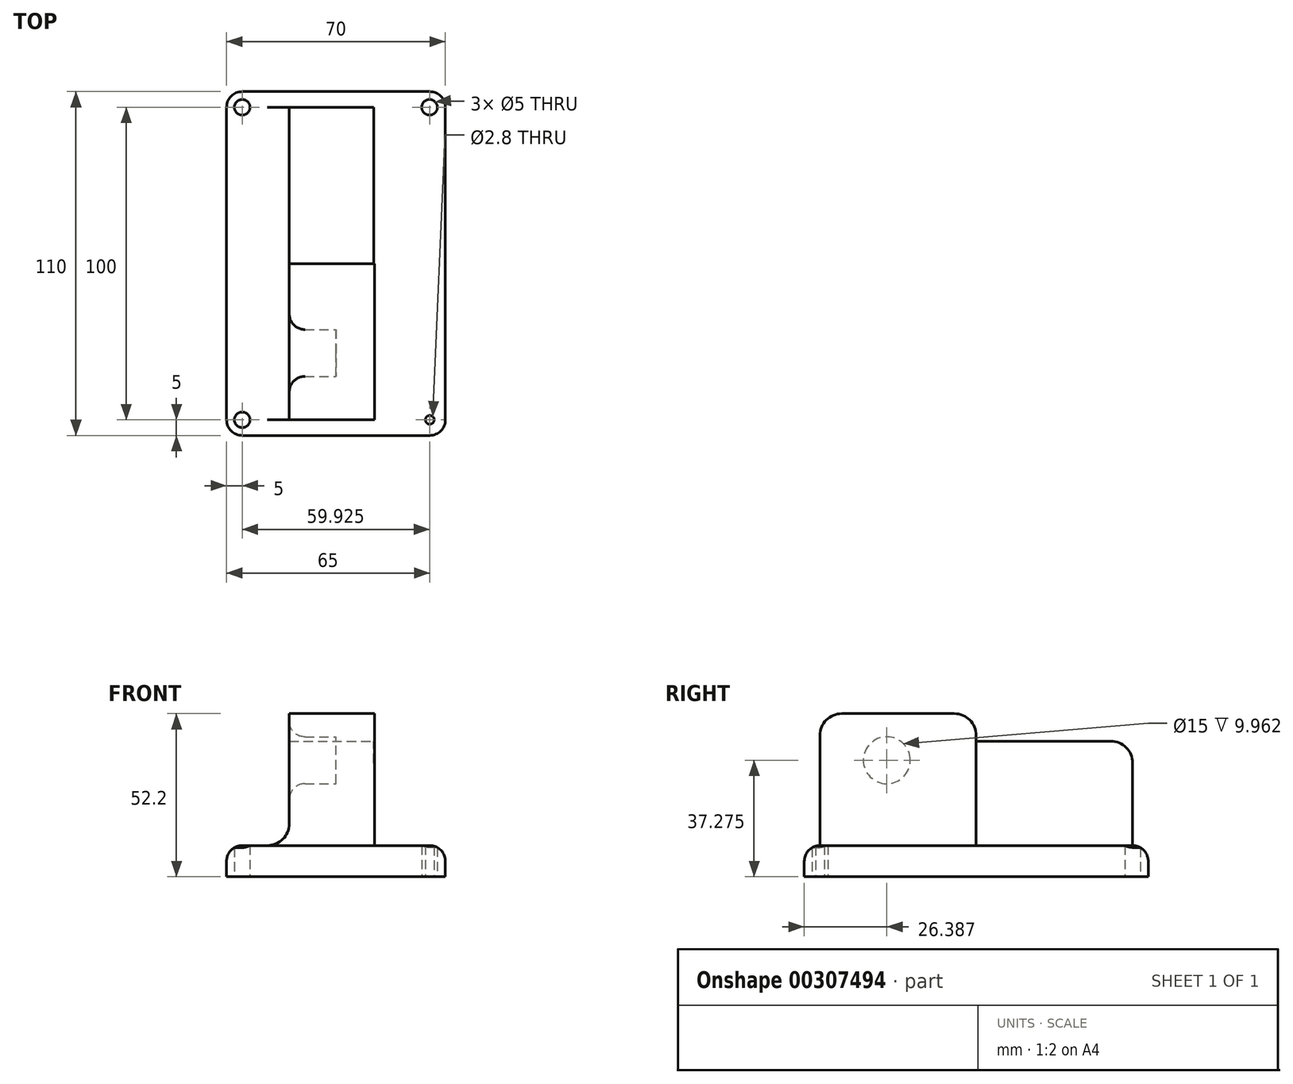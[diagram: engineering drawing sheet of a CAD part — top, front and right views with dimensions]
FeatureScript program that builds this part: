
annotation { "Feature Type Name" : "Feature", "Feature Type Description" : "" }
export const myFeature = defineFeature(function(context is Context, id is Id, definition is map)
    precondition{}
    {
        {
            var Q0;
            Q0=qCreatedBy(makeId("Top.planeOp"),FACE);
            var sketch = newSketch(context, id + "F0", { "sketchPlane" : qUnion([Q0])});
            skLineSegment(sketch, "E0.bottom", {"start": v(30, -55) * mm, "end": v(-30, -55) * mm});
            skLineSegment(sketch, "E0.top", {"start": v(30, 55) * mm, "end": v(-30, 55) * mm});
            skLineSegment(sketch, "E0.left", {"start": v(35, -50) * mm, "end": v(35, 50) * mm});
            skLineSegment(sketch, "E0.right", {"start": v(-35, -50) * mm, "end": v(-35, 50) * mm});
            skPoint(sketch, "E0.middle", {"position": v(0, 0) * mm});
            skPoint(sketch, "E1.visualSharp", {"position": v(-35, 55) * mm});
            skArc(sketch, "E1.filletArc", {"start": v(-30, 55) * mm, "mid": v(-33.54, 53.54) * mm, "end": v(-35, 50) * mm});
            skPoint(sketch, "E2.visualSharp", {"position": v(35, 55) * mm});
            skArc(sketch, "E2.filletArc", {"start": v(35, 50) * mm, "mid": v(33.54, 53.54) * mm, "end": v(30, 55) * mm});
            skPoint(sketch, "E3.visualSharp", {"position": v(35, -55) * mm});
            skArc(sketch, "E3.filletArc", {"start": v(30, -55) * mm, "mid": v(33.54, -53.54) * mm, "end": v(35, -50) * mm});
            skPoint(sketch, "E4.visualSharp", {"position": v(-35, -55) * mm});
            skArc(sketch, "E4.filletArc", {"start": v(-35, -50) * mm, "mid": v(-33.54, -53.54) * mm, "end": v(-30, -55) * mm});
            skLineSegment(sketch, "E5", {"start": v(-35, 50) * mm, "end": v(30, 50) * mm, "construction": true});
            skLineSegment(sketch, "E6", {"start": v(0, 0) * mm, "end": v(0, 50) * mm, "construction": true});
            skLineSegment(sketch, "E7", {"start": v(-30, -50) * mm, "end": v(30, -50) * mm, "construction": true});
            skLineSegment(sketch, "E8.bottom", {"start": v(-14.96, 50) * mm, "end": v(12.07, 50) * mm});
            skLineSegment(sketch, "E8.top", {"start": v(-14.96, 0) * mm, "end": v(12.07, 0) * mm});
            skLineSegment(sketch, "E8.left", {"start": v(-14.96, 50) * mm, "end": v(-14.96, 0) * mm});
            skLineSegment(sketch, "E8.right", {"start": v(12.07, 50) * mm, "end": v(12.07, 0) * mm});
            skLineSegment(sketch, "E9.bottom", {"start": v(-14.96, 0) * mm, "end": v(12.34, 0) * mm});
            skLineSegment(sketch, "E9.top", {"start": v(-14.96, -50) * mm, "end": v(12.34, -50) * mm});
            skLineSegment(sketch, "E9.left", {"start": v(-14.96, 0) * mm, "end": v(-14.96, -50) * mm});
            skLineSegment(sketch, "E9.right", {"start": v(12.34, 0) * mm, "end": v(12.34, -50) * mm});
            skCircle(sketch, "E10", {"center": v(-30, 50) * mm, "radius": 2.5 * mm});
            skCircle(sketch, "E11", {"center": v(29.92, 50) * mm, "radius": 2.5 * mm});
            skCircle(sketch, "E12", {"center": v(-30, -50) * mm, "radius": 2.5 * mm});
            skCircle(sketch, "E13", {"center": v(30, -50) * mm, "radius": 1.4 * mm});
            skSolve(sketch);
        }
        {
            var Q0;
            Q0=makeQuery(id+"F0.imprint","IMPRINT",FACE,{"disambiguationData":[TD([[makeQuery(id+"F0.imprint","IMPRINT",EDGE,{"derivedFrom":sQuery(id+"F0.wireOp",EDGE,"E0.bottom")}),-1.0]])]});
            extrude(context, id + "F1", {"entities" : qUnion([Q0]), "depth" : 10 * mm});
        }
        {
            var Q0;
            Q0=makeQuery(id+"F0.imprint","IMPRINT",FACE,{"disambiguationData":[TD([[makeQuery(id+"F0.imprint","IMPRINT",EDGE,{"derivedFrom":sQuery(id+"F0.wireOp",EDGE,"E8.bottom")}),-1.0]])]});
            extrude(context, id + "F2", {"entities" : qUnion([Q0]), "operationType" : NewBodyOperationType.ADD, "depth" : 43.4 * mm});
        }
        {
            var Q0;
            Q0=makeQuery(id+"F0.imprint","IMPRINT",FACE,{"disambiguationData":[TD([[makeQuery(id+"F0.imprint","IMPRINT",EDGE,{"derivedFrom":sQuery(id+"F0.wireOp",EDGE,"E9.top")}),1.0]])]});
            extrude(context, id + "F3", {"entities" : qUnion([Q0]), "operationType" : NewBodyOperationType.ADD, "depth" : 52.2 * mm});
        }
        {
            var Q0;
            Q0=makeQuery(id+"F3.opExtrude","CAP_EDGE",EDGE,{"disambiguationData":[OSD([sQuery(id+"F0.wireOp",EDGE,"E9.bottom")])],"isStart":false});
            var Q1;
            Q1=makeQuery(id+"F2.opExtrude","CAP_EDGE",EDGE,{"disambiguationData":[OSD([sQuery(id+"F0.wireOp",EDGE,"E8.bottom")])],"isStart":false});
            var Q2;
            Q2=makeQuery(id+"F3.opExtrude","CAP_EDGE",EDGE,{"disambiguationData":[OSD([sQuery(id+"F0.wireOp",EDGE,"E9.top")])],"isStart":false});
            var Q3;
            {var subQ0=sQuery(id+"F0.wireOp",EDGE,"E9.left");var subQ1=sQuery(id+"F0.wireOp",EDGE,"E8.left");var subQ3=makeQuery(id+"F1.opExtrude","CAP_EDGE",EDGE,{"disambiguationData":[OSD([subQ1,subQ0])],"isStart":false});Q3=makeQuery(id+"F3.boolean.opBoolean","MERGE",EDGE,{"derivedFrom":[makeQuery(id+"F2.boolean.opBoolean","SPLIT",EDGE,{"disambiguationData":[topologyDisambiguationEdgeConnected([makeQuery(id+"F1.opExtrude","SWEPT_FACE",FACE,{"disambiguationData":[OSD([subQ1,subQ0])]})])],"derivedFrom":subQ3}),makeQuery(id+"F2.boolean.opBoolean","SPLIT",EDGE,{"disambiguationData":[topologyDisambiguationEdgeConnected([makeQuery(id+"F2.opExtrude","SWEPT_FACE",FACE,{"disambiguationData":[OSD([subQ1])]})])],"derivedFrom":subQ3})]});}
            var Q4;
            Q4=makeQuery(id+"F1.opExtrude","CAP_EDGE",EDGE,{"disambiguationData":[OSD([sQuery(id+"F0.wireOp",EDGE,"E8.bottom")])],"isStart":false});
            fillet(context, id + "F4", {"entities" : qUnion([Q0, Q1, Q2, Q3, Q4]), "radius" : 7 * mm, "tangentPropagation" : true, "allowEdgeOverflow" : false});
        }
        {
            var Q0;
            Q0=qCreatedBy(makeId("Right.planeOp"),FACE);
            var sketch = newSketch(context, id + "F5", { "sketchPlane" : qUnion([Q0])});
            skCircle(sketch, "E14", {"center": v(-28.61, 37.28) * mm, "radius": 7.5 * mm});
            skSolve(sketch);
        }
        {
            var Q0;
            Q0 = qSketchRegion(id + "F5", true);
            extrude(context, id + "F6", {"entities" : qUnion([Q0]), "operationType" : NewBodyOperationType.REMOVE, "oppositeDirection" : true, "depth" : 40 * mm});
        }
        {
            var Q0;
            Q0=makeQuery(id+"F2.opExtrude","CAP_EDGE",EDGE,{"disambiguationData":[OSD([sQuery(id+"F0.wireOp",EDGE,"E8.bottom")])],"isStart":false});
            var Q1;
            Q1=makeQuery(id+"F1.opExtrude","CAP_EDGE",EDGE,{"disambiguationData":[OSD([sQuery(id+"F0.wireOp",EDGE,"E0.right")])],"isStart":false});
            var Q2;
            Q2=makeQuery(id+"F1.opExtrude","CAP_EDGE",EDGE,{"disambiguationData":[OSD([sQuery(id+"F0.wireOp",EDGE,"E0.top")])],"isStart":false});
            var Q3;
            Q3=makeQuery(id+"F6.boolean.opBoolean","INTERSECT",EDGE,{"derivedFrom":[makeQuery(id+"F3.boolean.opBoolean","MERGE",FACE,{"derivedFrom":[makeQuery(id+"F2.opExtrude","SWEPT_FACE",FACE,{"disambiguationData":[OSD([sQuery(id+"F0.wireOp",EDGE,"E8.left")])]}),makeQuery(id+"F3.opExtrude","SWEPT_FACE",FACE,{"disambiguationData":[OSD([sQuery(id+"F0.wireOp",EDGE,"E9.left")])]})]}),makeQuery(id+"F6.opExtrude","SWEPT_FACE",FACE,{"disambiguationData":[OSD([sQuery(id+"F5.wireOp",EDGE,"E14")])]})]});
            fillet(context, id + "F7", {"entities" : qUnion([Q0, Q1, Q2, Q3]), "radius" : 5 * mm, "tangentPropagation" : true, "allowEdgeOverflow" : false});
        }
    });
